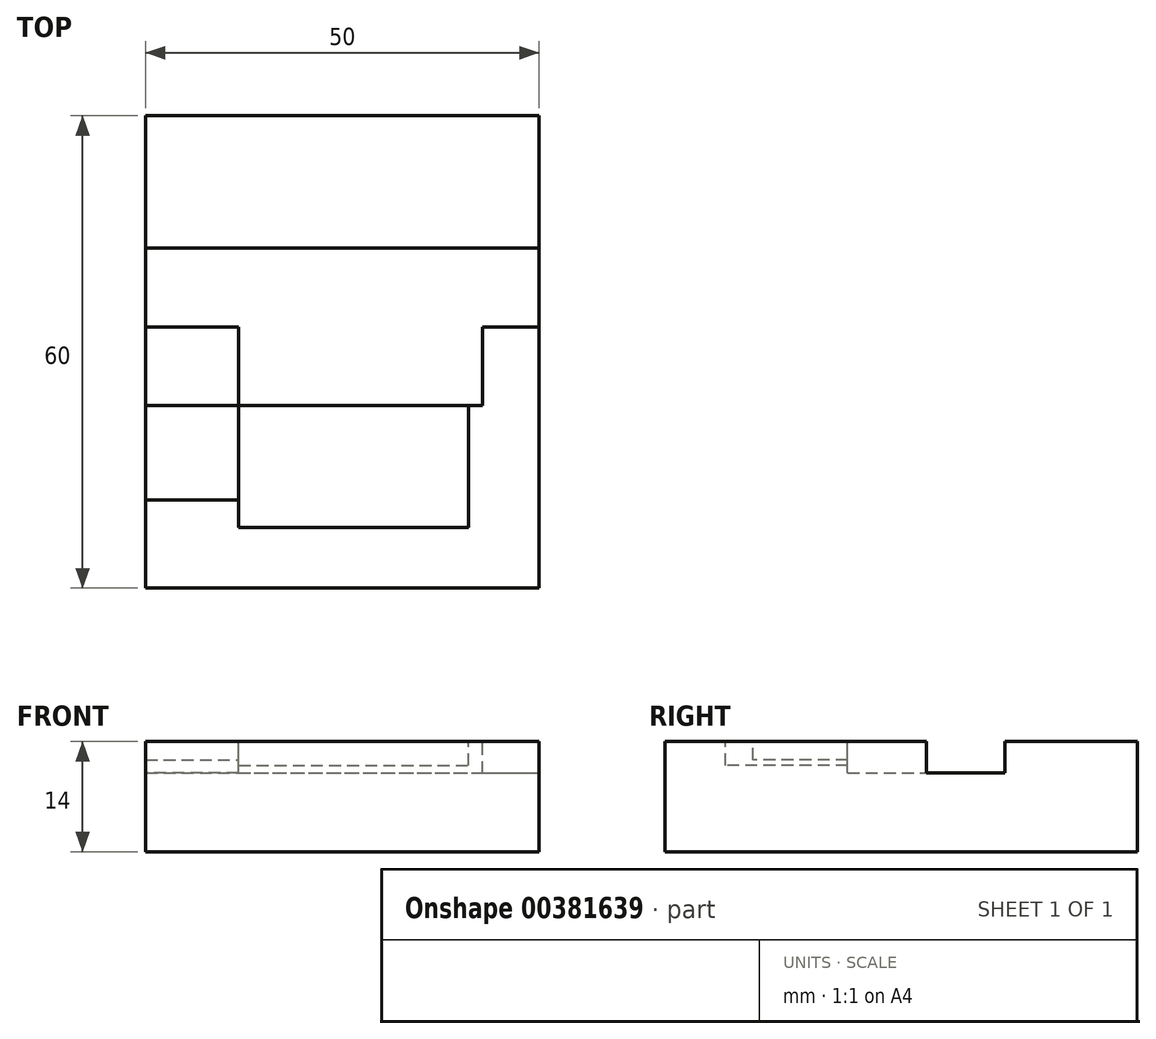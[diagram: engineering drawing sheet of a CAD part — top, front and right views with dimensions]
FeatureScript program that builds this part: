
annotation { "Feature Type Name" : "Feature", "Feature Type Description" : "" }
export const myFeature = defineFeature(function(context is Context, id is Id, definition is map)
    precondition{}
    {
        {
            var Q0;
            Q0=qCreatedBy(makeId("Top.planeOp"),FACE);
            var sketch = newSketch(context, id + "F0", { "sketchPlane" : qUnion([Q0])});
            skLineSegment(sketch, "E0.bottom", {"start": v(-25.1, 22.03) * mm, "end": v(24.9, 22.03) * mm});
            skLineSegment(sketch, "E0.top", {"start": v(-25.1, -37.97) * mm, "end": v(24.9, -37.97) * mm});
            skLineSegment(sketch, "E0.left", {"start": v(-25.1, 22.03) * mm, "end": v(-25.1, -37.97) * mm});
            skLineSegment(sketch, "E0.right", {"start": v(24.9, 22.03) * mm, "end": v(24.9, -37.97) * mm});
            skSolve(sketch);
        }
        {
            var Q0;
            Q0=makeQuery(id+"F0.imprint","IMPRINT",FACE,{"disambiguationData":[TD([[makeQuery(id+"F0.imprint","IMPRINT",EDGE,{"derivedFrom":sQuery(id+"F0.wireOp",EDGE,"E0.bottom")}),-1.0]])]});
            extrude(context, id + "F1", {"entities" : qUnion([Q0]), "depth" : 14 * mm});
        }
        {
            var Q0;
            Q0=makeQuery(id+"F1.opExtrude","CAP_FACE",FACE,{"disambiguationData":[OSD([sQuery(id+"F0.wireOp",EDGE,"E0.bottom"),sQuery(id+"F0.wireOp",EDGE,"E0.top"),sQuery(id+"F0.wireOp",EDGE,"E0.left"),sQuery(id+"F0.wireOp",EDGE,"E0.right")])],"isStart":false});
            var sketch = newSketch(context, id + "F2", { "sketchPlane" : qUnion([Q0])});
            skLineSegment(sketch, "E1.bottom", {"start": v(-13.28, -14.79) * mm, "end": v(15.92, -14.79) * mm});
            skLineSegment(sketch, "E1.top", {"start": v(-13.28, -30.29) * mm, "end": v(15.92, -30.29) * mm});
            skLineSegment(sketch, "E1.left", {"start": v(-13.28, -14.79) * mm, "end": v(-13.28, -30.29) * mm});
            skLineSegment(sketch, "E1.right", {"start": v(15.92, -14.79) * mm, "end": v(15.92, -30.29) * mm});
            skSolve(sketch);
        }
        {
            var Q0;
            Q0=makeQuery(id+"F2.imprint","IMPRINT",FACE,{"disambiguationData":[TD([[makeQuery(id+"F2.imprint","IMPRINT",EDGE,{"derivedFrom":sQuery(id+"F2.wireOp",EDGE,"E1.bottom")}),-1.0]])]});
            extrude(context, id + "F3", {"entities" : qUnion([Q0]), "operationType" : NewBodyOperationType.REMOVE, "oppositeDirection" : true, "depth" : 3 * mm});
        }
        {
            var Q0;
            Q0=makeQuery(id+"F1.opExtrude","CAP_FACE",FACE,{"disambiguationData":[OSD([sQuery(id+"F0.wireOp",EDGE,"E0.bottom"),sQuery(id+"F0.wireOp",EDGE,"E0.top"),sQuery(id+"F0.wireOp",EDGE,"E0.left"),sQuery(id+"F0.wireOp",EDGE,"E0.right")])],"isStart":false});
            var sketch = newSketch(context, id + "F4", { "sketchPlane" : qUnion([Q0])});
            skLineSegment(sketch, "E2.bottom", {"start": v(-25.1, -14.79) * mm, "end": v(-13.28, -14.79) * mm});
            skLineSegment(sketch, "E2.top", {"start": v(-25.1, -26.79) * mm, "end": v(-13.28, -26.79) * mm});
            skLineSegment(sketch, "E2.left", {"start": v(-25.1, -14.79) * mm, "end": v(-25.1, -26.79) * mm});
            skLineSegment(sketch, "E2.right", {"start": v(-13.28, -14.79) * mm, "end": v(-13.28, -26.79) * mm});
            skSolve(sketch);
        }
        {
            var Q0;
            Q0=makeQuery(id+"F4.imprint","IMPRINT",FACE,{"disambiguationData":[TD([[makeQuery(id+"F4.imprint","IMPRINT",EDGE,{"derivedFrom":sQuery(id+"F4.wireOp",EDGE,"E2.bottom")}),-1.0]])]});
            extrude(context, id + "F5", {"entities" : qUnion([Q0]), "operationType" : NewBodyOperationType.REMOVE, "oppositeDirection" : true, "depth" : 2.3 * mm});
        }
        {
            var Q0;
            Q0=makeQuery(id+"F1.opExtrude","CAP_FACE",FACE,{"disambiguationData":[OSD([sQuery(id+"F0.wireOp",EDGE,"E0.bottom"),sQuery(id+"F0.wireOp",EDGE,"E0.top"),sQuery(id+"F0.wireOp",EDGE,"E0.left"),sQuery(id+"F0.wireOp",EDGE,"E0.right")])],"isStart":false});
            var sketch = newSketch(context, id + "F6", { "sketchPlane" : qUnion([Q0])});
            skLineSegment(sketch, "E3.bottom", {"start": v(-13.28, -14.79) * mm, "end": v(17.72, -14.79) * mm});
            skLineSegment(sketch, "E3.top", {"start": v(-13.28, 5.21) * mm, "end": v(17.72, 5.21) * mm});
            skLineSegment(sketch, "E3.left", {"start": v(-13.28, -14.79) * mm, "end": v(-13.28, -4.79) * mm});
            skLineSegment(sketch, "E3.right", {"start": v(17.72, -14.79) * mm, "end": v(17.72, -4.79) * mm});
            skLineSegment(sketch, "E4.bottom", {"start": v(17.72, 5.21) * mm, "end": v(24.9, 5.21) * mm});
            skLineSegment(sketch, "E4.top", {"start": v(17.72, -4.79) * mm, "end": v(24.9, -4.79) * mm});
            skLineSegment(sketch, "E4.right", {"start": v(24.9, 5.21) * mm, "end": v(24.9, -4.79) * mm});
            skLineSegment(sketch, "E5.bottom", {"start": v(-13.28, 5.21) * mm, "end": v(-25.1, 5.21) * mm});
            skLineSegment(sketch, "E5.top", {"start": v(-13.28, -4.79) * mm, "end": v(-25.1, -4.79) * mm});
            skLineSegment(sketch, "E5.right", {"start": v(-25.1, 5.21) * mm, "end": v(-25.1, -4.79) * mm});
            skSolve(sketch);
        }
        {
            var Q0;
            Q0=makeQuery(id+"F6.imprint","IMPRINT",FACE,{"disambiguationData":[TD([[makeQuery(id+"F6.imprint","IMPRINT",EDGE,{"derivedFrom":sQuery(id+"F6.wireOp",EDGE,"E3.top")}),-1.0]])]});
            extrude(context, id + "F7", {"entities" : qUnion([Q0]), "operationType" : NewBodyOperationType.REMOVE, "oppositeDirection" : true, "depth" : 4 * mm});
        }
    });
